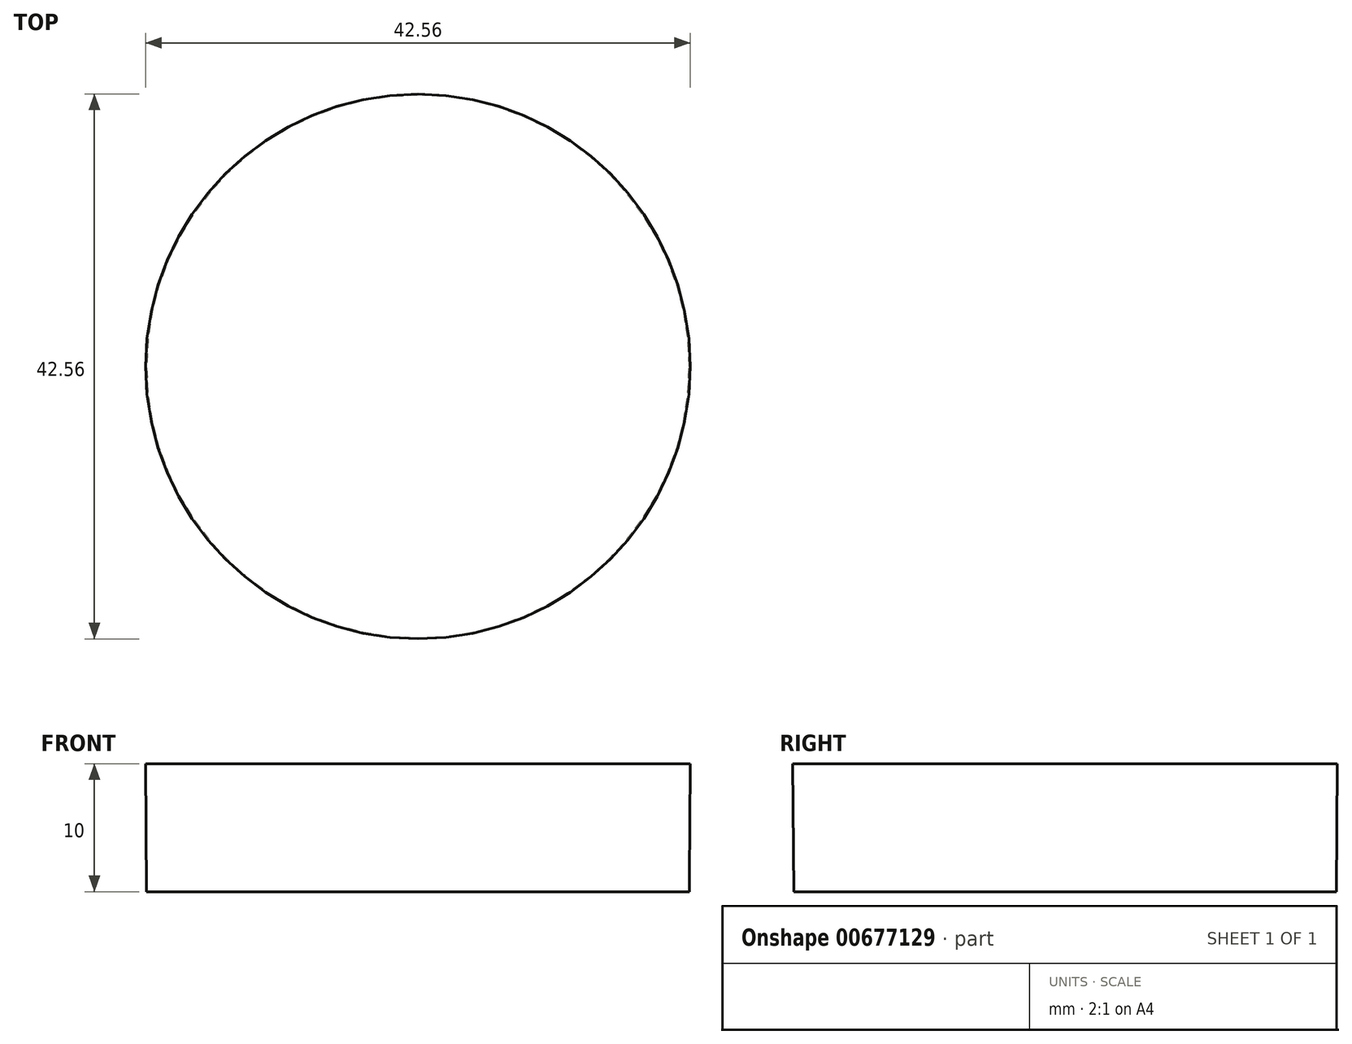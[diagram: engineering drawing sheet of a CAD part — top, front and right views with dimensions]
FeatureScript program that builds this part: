
annotation { "Feature Type Name" : "Feature", "Feature Type Description" : "" }
export const myFeature = defineFeature(function(context is Context, id is Id, definition is map)
    precondition{}
    {
        {
            var Q0;
            Q0=qCreatedBy(makeId("Top.planeOp"),FACE);
            var sketch = newSketch(context, id + "F0", { "sketchPlane" : qUnion([Q0])});
            skCircle(sketch, "E0", {"center": v(0, 0) * mm, "radius": 21.2 * mm});
            skSolve(sketch);
        }
        {
            var Q0;
            Q0=qCreatedBy(makeId("Top.planeOp"),FACE);
            cPlane(context, id + "F1", {"entities" : qUnion([Q0]), "cplaneType" : CPlaneType.OFFSET, "offset" : 10 * mm, "width" : 150 * mm, "height" : 150 * mm});
        }
        {
            var Q0;
            Q0=qCreatedBy(id+"F1.planeOp",FACE);
            var sketch = newSketch(context, id + "F2", { "sketchPlane" : qUnion([Q0])});
            skCircle(sketch, "E1", {"center": v(0, 0) * mm, "radius": 21.27 * mm});
            skSolve(sketch);
        }
        {
            var Q0;
            Q0=makeQuery(id+"F2.imprint","IMPRINT",FACE,{"disambiguationData":[TD([[makeQuery(id+"F2.imprint","IMPRINT",EDGE,{"derivedFrom":sQuery(id+"F2.wireOp",EDGE,"E1")}),1.0]])]});
            var Q1;
            Q1=makeQuery(id+"F0.imprint","IMPRINT",FACE,{"disambiguationData":[TD([[makeQuery(id+"F0.imprint","IMPRINT",EDGE,{"derivedFrom":sQuery(id+"F0.wireOp",EDGE,"E0")}),1.0]])]});
            loft(context, id + "F3", {"sheetProfilesArray" : [{ "sheetProfileEntities" : qUnion([Q0]) }, { "sheetProfileEntities" : qUnion([Q1]) }]});
        }
    });
